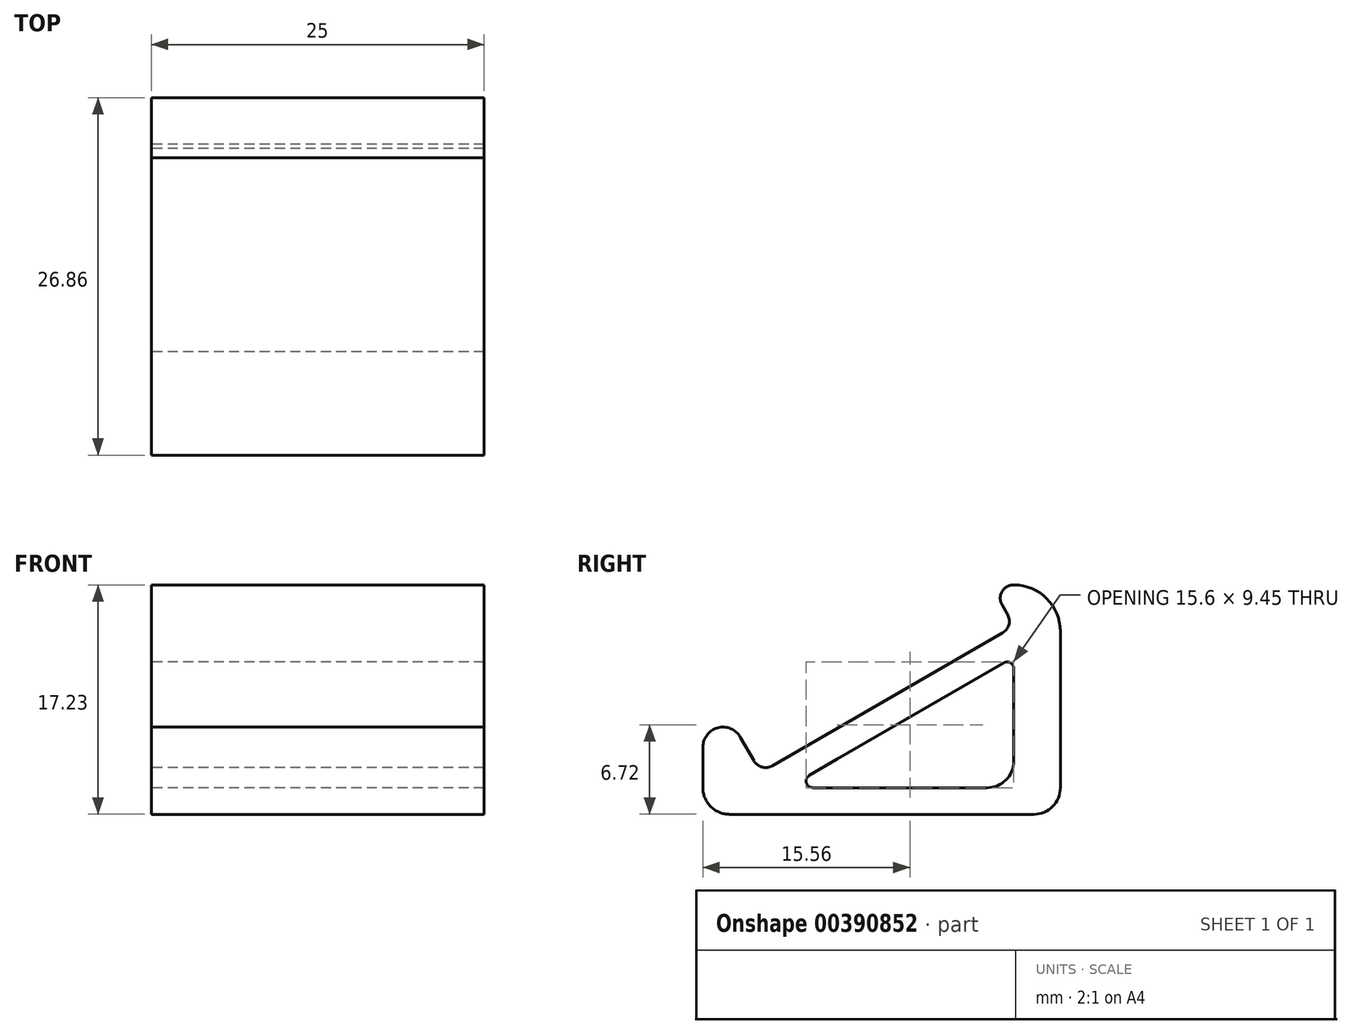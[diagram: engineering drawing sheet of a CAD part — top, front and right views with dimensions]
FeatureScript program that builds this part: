
annotation { "Feature Type Name" : "Feature", "Feature Type Description" : "" }
export const myFeature = defineFeature(function(context is Context, id is Id, definition is map)
    precondition{}
    {
        {
            var Q0;
            Q0=qCreatedBy(makeId("Right.planeOp"),FACE);
            var sketch = newSketch(context, id + "F0", { "sketchPlane" : qUnion([Q0])});
            skLineSegment(sketch, "E0", {"start": v(10.1, 0.8) * mm, "end": v(10.1, 7.75) * mm});
            skLineSegment(sketch, "E1", {"start": v(9.27, 10.44) * mm, "end": v(-8.05, 0.44) * mm});
            skLineSegment(sketch, "E2", {"start": v(9.63, 11.8) * mm, "end": v(9.21, 12.53) * mm});
            skLineSegment(sketch, "E3", {"start": v(-9.42, 0.8) * mm, "end": v(-10.45, 2.6) * mm});
            skLineSegment(sketch, "E4", {"start": v(-13.25, 1.85) * mm, "end": v(-13.26, -1.2) * mm});
            skLineSegment(sketch, "E5", {"start": v(-11.26, -3.2) * mm, "end": v(11.6, -3.2) * mm});
            skPoint(sketch, "E6.visualSharp", {"position": v(-13.26, -3.2) * mm});
            skArc(sketch, "E6.filletArc", {"start": v(-13.26, -1.2) * mm, "mid": v(-12.67, -2.62) * mm, "end": v(-11.26, -3.2) * mm});
            skPoint(sketch, "E7.visualSharp", {"position": v(-13.25, 7.44) * mm});
            skArc(sketch, "E7.filletArc", {"start": v(-10.45, 2.6) * mm, "mid": v(-12.14, 3.3) * mm, "end": v(-13.25, 1.85) * mm});
            skPoint(sketch, "E8.visualSharp", {"position": v(8.4, 13.94) * mm});
            skLineSegment(sketch, "E9", {"start": v(13.6, -1.2) * mm, "end": v(13.6, 10.53) * mm});
            skLineSegment(sketch, "E10", {"start": v(10.08, 14.03) * mm, "end": v(10.1, 14.03) * mm});
            skPoint(sketch, "E11.visualSharp", {"position": v(13.6, 14.03) * mm});
            skArc(sketch, "E11.filletArc", {"start": v(13.6, 10.53) * mm, "mid": v(12.57, 13) * mm, "end": v(10.1, 14.03) * mm});
            skPoint(sketch, "E12.visualSharp", {"position": v(8.35, 14.03) * mm});
            skArc(sketch, "E12.filletArc", {"start": v(10.08, 14.03) * mm, "mid": v(9.21, 13.53) * mm, "end": v(9.21, 12.53) * mm});
            skLineSegment(sketch, "E13", {"start": v(9.35, 8.18) * mm, "end": v(-1.58, 1.87) * mm});
            skPoint(sketch, "E14.newPointB", {"position": v(-8.95, 0) * mm});
            skPoint(sketch, "E15.newPointB", {"position": v(10.1, 11) * mm});
            skLineSegment(sketch, "E15.filletArc", {"start": v(10.1, 8.61) * mm, "end": v(10.1, 8.61) * mm});
            skPoint(sketch, "E16.visualSharp", {"position": v(10.1, 0) * mm});
            skPoint(sketch, "E17.visualSharp", {"position": v(-8.92, -0.06) * mm});
            skArc(sketch, "E17.filletArc", {"start": v(-9.42, 0.8) * mm, "mid": v(-8.81, 0.34) * mm, "end": v(-8.05, 0.44) * mm});
            skPoint(sketch, "E18.visualSharp", {"position": v(10.13, 10.94) * mm});
            skArc(sketch, "E18.filletArc", {"start": v(9.27, 10.44) * mm, "mid": v(9.73, 11.05) * mm, "end": v(9.63, 11.8) * mm});
            skPoint(sketch, "E19.visualSharp", {"position": v(13.6, -3.2) * mm});
            skArc(sketch, "E19.filletArc", {"start": v(11.6, -3.2) * mm, "mid": v(13.01, -2.62) * mm, "end": v(13.6, -1.2) * mm});
            skLineSegment(sketch, "E20", {"start": v(-1.58, 1.87) * mm, "end": v(-3.2, 0.93) * mm});
            skArc(sketch, "E21.filletArc", {"start": v(10.1, 7.75) * mm, "mid": v(9.85, 8.18) * mm, "end": v(9.35, 8.18) * mm});
            skPoint(sketch, "E22.visualSharp", {"position": v(-4.82, 0) * mm});
            skLineSegment(sketch, "E23", {"start": v(8.1, -1.2) * mm, "end": v(-5, -1.2) * mm});
            skLineSegment(sketch, "E24", {"start": v(-3.2, 0.93) * mm, "end": v(-5.25, -0.27) * mm});
            skPoint(sketch, "E25.visualSharp", {"position": v(-6.84, -1.2) * mm});
            skArc(sketch, "E25.filletArc", {"start": v(-5.25, -0.27) * mm, "mid": v(-5.48, -0.84) * mm, "end": v(-5, -1.2) * mm});
            skPoint(sketch, "E26.visualSharp", {"position": v(10.1, -1.2) * mm});
            skArc(sketch, "E26.filletArc", {"start": v(8.1, -1.2) * mm, "mid": v(9.51, -0.62) * mm, "end": v(10.1, 0.8) * mm});
            skSolve(sketch);
        }
        {
            var Q0;
            Q0=makeQuery(id+"F0.imprint","IMPRINT",FACE,{"disambiguationData":[TD([[makeQuery(id+"F0.imprint","IMPRINT",EDGE,{"derivedFrom":sQuery(id+"F0.wireOp",EDGE,"E0")}),-1.0]])]});
            extrude(context, id + "F1", {"entities" : qUnion([Q0]), "depth" : 12.5 * mm, "offsetDistance" : 25 * mm, "hasSecondDirection" : true, "secondDirectionOppositeDirection" : true, "secondDirectionDepth" : 12.5 * mm});
        }
    });
